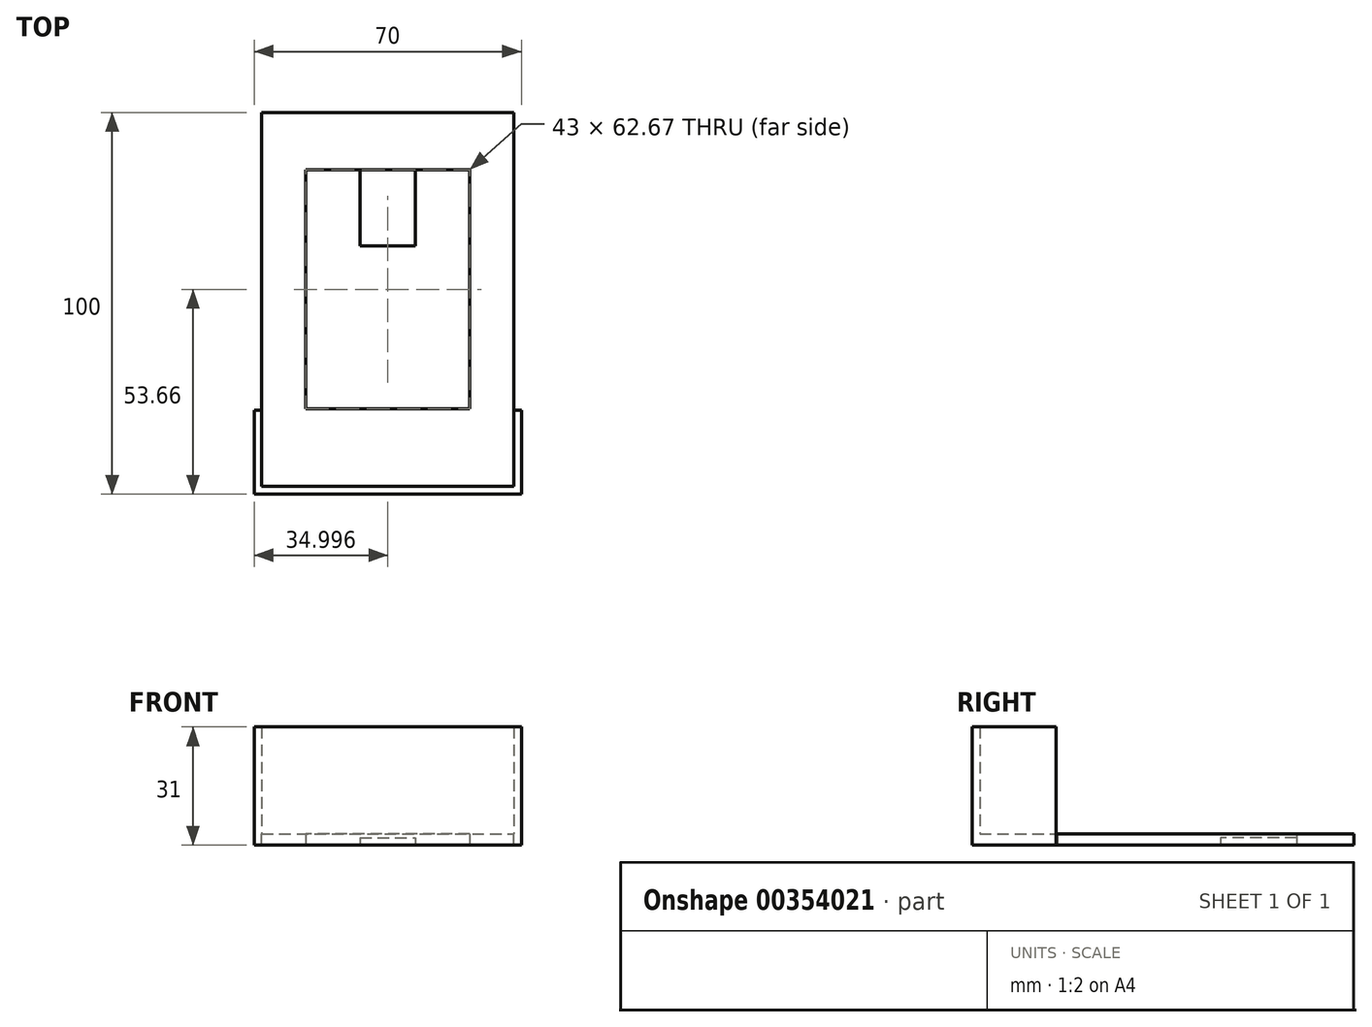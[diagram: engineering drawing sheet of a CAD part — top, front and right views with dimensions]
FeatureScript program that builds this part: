
annotation { "Feature Type Name" : "Feature", "Feature Type Description" : "" }
export const myFeature = defineFeature(function(context is Context, id is Id, definition is map)
    precondition{}
    {
        {
            var Q0;
            Q0=qCreatedBy(makeId("Top.planeOp"),FACE);
            var sketch = newSketch(context, id + "F0", { "sketchPlane" : qUnion([Q0])});
            skLineSegment(sketch, "E0.bottom", {"start": v(-60.66, 56.66) * mm, "end": v(9.34, 56.66) * mm});
            skLineSegment(sketch, "E0.top", {"start": v(-60.66, -43.34) * mm, "end": v(9.34, -43.34) * mm});
            skLineSegment(sketch, "E0.left", {"start": v(-60.66, 56.66) * mm, "end": v(-60.66, -43.34) * mm});
            skLineSegment(sketch, "E0.right", {"start": v(9.34, 56.66) * mm, "end": v(9.34, -43.34) * mm});
            skSolve(sketch);
        }
        {
            var Q0;
            Q0 = qSketchRegion(id + "F0", true);
            extrude(context, id + "F1", {"entities" : qUnion([Q0]), "depth" : 3 * mm});
        }
        {
            var Q0;
            Q0=makeQuery(id+"F1.opExtrude","CAP_FACE",FACE,{"disambiguationData":[OSD([sQuery(id+"F0.wireOp",EDGE,"E0.bottom"),sQuery(id+"F0.wireOp",EDGE,"E0.top"),sQuery(id+"F0.wireOp",EDGE,"E0.left"),sQuery(id+"F0.wireOp",EDGE,"E0.right")])],"isStart":false});
            var sketch = newSketch(context, id + "F2", { "sketchPlane" : qUnion([Q0])});
            skLineSegment(sketch, "E1.0", {"start": v(-60.66, -43.34) * mm, "end": v(9.34, -43.34) * mm});
            skPoint(sketch, "E2.0.start.orphan", {"position": v(-60.66, 56.66) * mm});
            skLineSegment(sketch, "E3", {"start": v(-60.66, -43.34) * mm, "end": v(-60.66, -21.34) * mm});
            skLineSegment(sketch, "E4", {"start": v(9.34, -43.34) * mm, "end": v(9.34, -21.34) * mm});
            skLineSegment(sketch, "E5.0", {"start": v(7.34, -41.34) * mm, "end": v(7.34, -21.34) * mm});
            skLineSegment(sketch, "E5.1", {"start": v(-58.66, -41.34) * mm, "end": v(7.34, -41.34) * mm});
            skLineSegment(sketch, "E5.2", {"start": v(-58.66, -41.34) * mm, "end": v(-58.66, -21.34) * mm});
            skLineSegment(sketch, "E6", {"start": v(9.34, -21.34) * mm, "end": v(7.34, -21.34) * mm});
            skLineSegment(sketch, "E7.trimOffspring", {"start": v(-58.66, -21.34) * mm, "end": v(-60.66, -21.34) * mm});
            skSolve(sketch);
        }
        {
            var Q0;
            Q0 = qSketchRegion(id + "F2", true);
            extrude(context, id + "F3", {"entities" : qUnion([Q0]), "operationType" : NewBodyOperationType.ADD, "depth" : 28 * mm});
        }
        {
            var Q0;
            Q0=makeQuery(id+"F1.opExtrude","CAP_FACE",FACE,{"disambiguationData":[OSD([sQuery(id+"F0.wireOp",EDGE,"E0.bottom"),sQuery(id+"F0.wireOp",EDGE,"E0.top"),sQuery(id+"F0.wireOp",EDGE,"E0.left"),sQuery(id+"F0.wireOp",EDGE,"E0.right")])],"isStart":false});
            var sketch = newSketch(context, id + "F4", { "sketchPlane" : qUnion([Q0])});
            skLineSegment(sketch, "E8", {"start": v(7.34, -21.34) * mm, "end": v(7.34, 56.66) * mm});
            skLineSegment(sketch, "E9", {"start": v(-58.66, -21.34) * mm, "end": v(-58.66, 56.66) * mm});
            skLineSegment(sketch, "E10.0", {"start": v(-58.66, -21.34) * mm, "end": v(-60.66, -21.34) * mm});
            skLineSegment(sketch, "E11.0", {"start": v(-60.66, 56.66) * mm, "end": v(-60.66, -21.34) * mm});
            skLineSegment(sketch, "E12.0", {"start": v(-60.66, 56.66) * mm, "end": v(-58.66, 56.66) * mm});
            skLineSegment(sketch, "E13.0", {"start": v(9.34, -21.34) * mm, "end": v(7.34, -21.34) * mm});
            skLineSegment(sketch, "E14.0", {"start": v(9.34, 56.66) * mm, "end": v(9.34, -21.34) * mm});
            skLineSegment(sketch, "E15.trimOffspring", {"start": v(7.34, 56.66) * mm, "end": v(9.34, 56.66) * mm});
            skSolve(sketch);
        }
        {
            var Q0;
            Q0 = qSketchRegion(id + "F4", true);
            extrude(context, id + "F5", {"entities" : qUnion([Q0]), "operationType" : NewBodyOperationType.REMOVE, "oppositeDirection" : true, "depth" : 30.6 * mm});
        }
        {
            var Q0;
            Q0=makeQuery(id+"F1.opExtrude","CAP_FACE",FACE,{"disambiguationData":[OSD([sQuery(id+"F0.wireOp",EDGE,"E0.bottom"),sQuery(id+"F0.wireOp",EDGE,"E0.top"),sQuery(id+"F0.wireOp",EDGE,"E0.left"),sQuery(id+"F0.wireOp",EDGE,"E0.right")])],"isStart":true});
            var sketch = newSketch(context, id + "F6", { "sketchPlane" : qUnion([Q0])});
            skLineSegment(sketch, "E16.0.0", {"start": v(-60.66, 21.34) * mm, "end": v(-58.66, 21.34) * mm});
            skLineSegment(sketch, "E16.0.1", {"start": v(-58.66, 21.34) * mm, "end": v(-58.66, -56.66) * mm});
            skLineSegment(sketch, "E16.0.2", {"start": v(-58.66, -56.66) * mm, "end": v(7.34, -56.66) * mm});
            skLineSegment(sketch, "E16.0.3", {"start": v(7.34, -56.66) * mm, "end": v(7.34, 21.34) * mm});
            skLineSegment(sketch, "E16.0.4", {"start": v(7.34, 21.34) * mm, "end": v(9.34, 21.34) * mm});
            skLineSegment(sketch, "E16.0.5", {"start": v(9.34, 21.34) * mm, "end": v(9.34, 43.34) * mm});
            skLineSegment(sketch, "E16.0.6", {"start": v(9.34, 43.34) * mm, "end": v(-60.66, 43.34) * mm});
            skLineSegment(sketch, "E16.0.7", {"start": v(-60.66, 43.34) * mm, "end": v(-60.66, 21.34) * mm});
            skLineSegment(sketch, "E17.bottom", {"start": v(-47.16, 21.02) * mm, "end": v(-4.16, 21.02) * mm});
            skLineSegment(sketch, "E17.left", {"start": v(-47.16, 21.02) * mm, "end": v(-47.16, -41.66) * mm});
            skLineSegment(sketch, "E17.right", {"start": v(-4.16, 21.02) * mm, "end": v(-4.16, -41.66) * mm});
            skPoint(sketch, "E17.middle", {"position": v(-25.66, -17.66) * mm});
            skLineSegment(sketch, "E18", {"start": v(-47.16, -41.66) * mm, "end": v(-32.91, -41.66) * mm});
            skLineSegment(sketch, "E19", {"start": v(-25.66, -21.66) * mm, "end": v(-18.41, -21.66) * mm});
            skLineSegment(sketch, "E20", {"start": v(-18.41, -21.66) * mm, "end": v(-32.91, -21.66) * mm});
            skLineSegment(sketch, "E21", {"start": v(-32.91, -21.66) * mm, "end": v(-32.91, -41.66) * mm});
            skLineSegment(sketch, "E22", {"start": v(-18.41, -41.66) * mm, "end": v(-18.41, -21.66) * mm});
            skLineSegment(sketch, "E23.trimOffspring", {"start": v(-18.41, -41.66) * mm, "end": v(-4.16, -41.66) * mm});
            skSolve(sketch);
        }
        {
            var Q0;
            Q0=makeQuery(id+"F6.imprint","IMPRINT",FACE,{"disambiguationData":[TD([[makeQuery(id+"F6.imprint","IMPRINT",EDGE,{"derivedFrom":sQuery(id+"F6.wireOp",EDGE,"E17.bottom")}),-1.0]])]});
            extrude(context, id + "F7", {"entities" : qUnion([Q0]), "operationType" : NewBodyOperationType.REMOVE, "oppositeDirection" : true, "depth" : 25 * mm});
        }
        {
            var Q0;
            Q0=makeQuery(id+"F1.opExtrude","CAP_FACE",FACE,{"disambiguationData":[OSD([sQuery(id+"F0.wireOp",EDGE,"E0.bottom"),sQuery(id+"F0.wireOp",EDGE,"E0.top"),sQuery(id+"F0.wireOp",EDGE,"E0.left"),sQuery(id+"F0.wireOp",EDGE,"E0.right")])],"isStart":false});
            var sketch = newSketch(context, id + "F8", { "sketchPlane" : qUnion([Q0])});
            skLineSegment(sketch, "E24", {"start": v(-32.91, 41.66) * mm, "end": v(-18.41, 41.66) * mm});
            skLineSegment(sketch, "E25.0", {"start": v(-18.41, 21.66) * mm, "end": v(-18.41, 41.66) * mm});
            skLineSegment(sketch, "E26.0", {"start": v(-32.91, 21.66) * mm, "end": v(-18.41, 21.66) * mm});
            skLineSegment(sketch, "E27.0", {"start": v(-32.91, 41.66) * mm, "end": v(-32.91, 21.66) * mm});
            skSolve(sketch);
        }
        {
            var Q0;
            Q0 = qSketchRegion(id + "F8", true);
            extrude(context, id + "F9", {"entities" : qUnion([Q0]), "operationType" : NewBodyOperationType.REMOVE, "oppositeDirection" : true, "depth" : 1 * mm});
        }
    });
